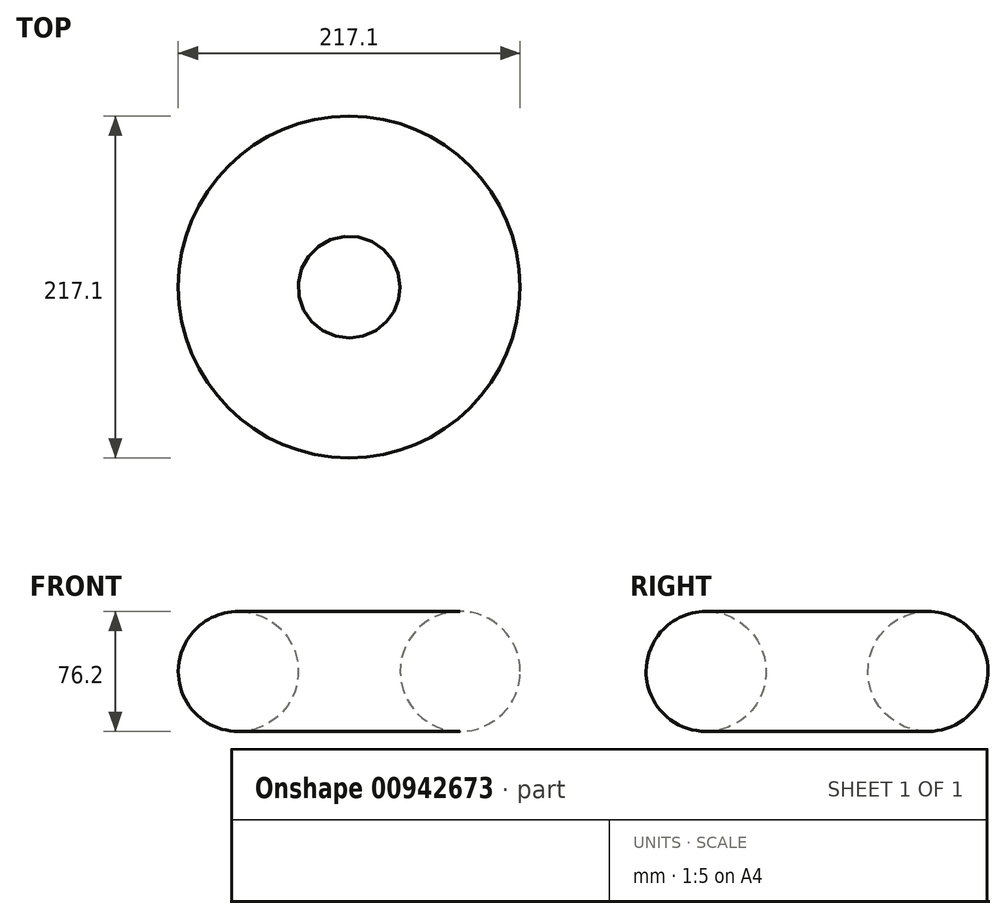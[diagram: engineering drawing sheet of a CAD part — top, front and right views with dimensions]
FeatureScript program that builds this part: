
annotation { "Feature Type Name" : "Feature", "Feature Type Description" : "" }
export const myFeature = defineFeature(function(context is Context, id is Id, definition is map)
    precondition{}
    {
        {
            var Q0;
            Q0=qCreatedBy(makeId("Front.planeOp"),FACE);
            var sketch = newSketch(context, id + "F0", { "sketchPlane" : qUnion([Q0])});
            skLineSegment(sketch, "E0", {"start": v(0, 24.2) * mm, "end": v(0, -27.7) * mm, "construction": true});
            skLineSegment(sketch, "E1", {"start": v(-98.7, 0) * mm, "end": v(104.5, 0) * mm});
            skCircle(sketch, "E2", {"center": v(-70.45, 0) * mm, "radius": 38.1 * mm});
            skLineSegment(sketch, "E3", {"start": v(105.17, 17.4) * mm, "end": v(104.5, -21.77) * mm, "construction": true});
            skSolve(sketch);
        }
        {
            var Q0;
            Q0 = qSketchRegion(id + "F0", true);
            var Q1;
            Q1=sQuery(id+"F0.wireOp",EDGE,"E0");
            revolve(context, id + "F1", {"surfaceOperationType" : NewSurfaceOperationType.NEW, "entities" : qUnion([Q0]), "axis" : qUnion([Q1]), "revolveType" : RevolveType.FULL});
        }
    });
